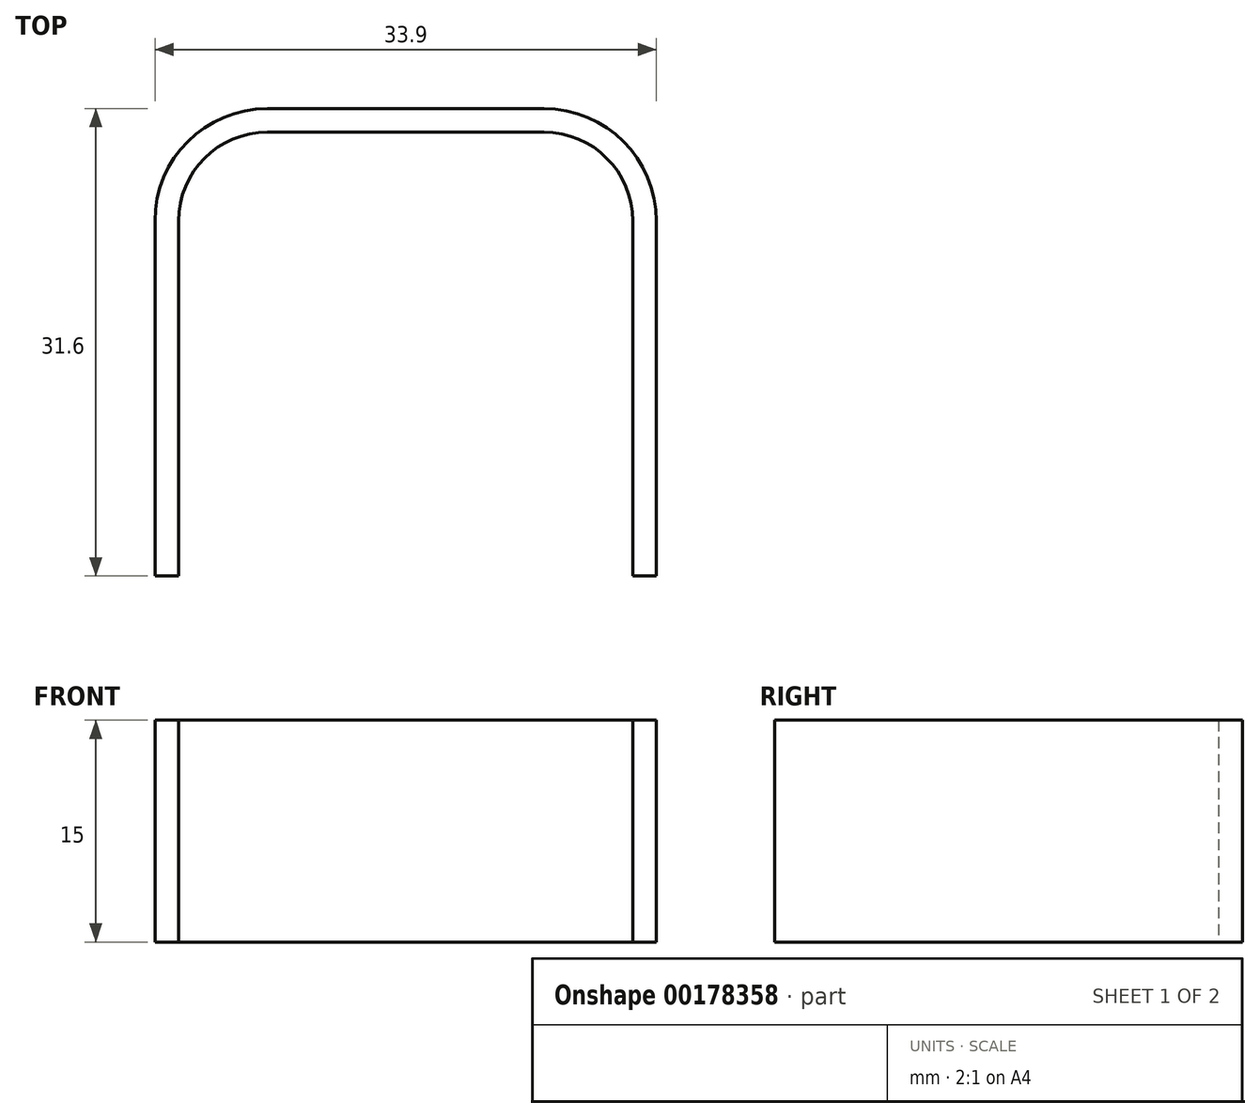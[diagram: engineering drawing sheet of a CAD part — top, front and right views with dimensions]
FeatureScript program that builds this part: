
annotation { "Feature Type Name" : "Feature", "Feature Type Description" : "" }
export const myFeature = defineFeature(function(context is Context, id is Id, definition is map)
    precondition{}
    {
        {
            var Q0;
            Q0=qCreatedBy(makeId("Top.planeOp"),FACE);
            var sketch = newSketch(context, id + "F0", { "sketchPlane" : qUnion([Q0])});
            skLineSegment(sketch, "E0", {"start": v(-15.35, -15.8) * mm, "end": v(-15.35, 14.2) * mm});
            skLineSegment(sketch, "E1", {"start": v(-15.35, 14.2) * mm, "end": v(15.35, 14.2) * mm});
            skLineSegment(sketch, "E2", {"start": v(15.35, 14.2) * mm, "end": v(15.35, -15.8) * mm});
            skLineSegment(sketch, "E3.0", {"start": v(16.95, 15.8) * mm, "end": v(16.95, -15.8) * mm});
            skLineSegment(sketch, "E3.1", {"start": v(-16.95, 15.8) * mm, "end": v(16.95, 15.8) * mm});
            skLineSegment(sketch, "E3.2", {"start": v(-16.95, -15.8) * mm, "end": v(-16.95, 15.8) * mm});
            skPoint(sketch, "E4", {"position": v(0, 15.8) * mm});
            skPoint(sketch, "E5", {"position": v(16.95, 0) * mm});
            skLineSegment(sketch, "E6", {"start": v(-16.95, -15.8) * mm, "end": v(-15.35, -15.8) * mm});
            skLineSegment(sketch, "E7", {"start": v(15.35, -15.8) * mm, "end": v(16.95, -15.8) * mm});
            skSolve(sketch);
        }
        {
            var Q0;
            Q0 = qSketchRegion(id + "F0", true);
            extrude(context, id + "F1", {"entities" : qUnion([Q0]), "depth" : 15 * mm, "offsetDistance" : 25 * mm});
        }
        {
            var Q0;
            Q0=makeQuery(id+"F1.opExtrude","SWEPT_EDGE",EDGE,{"disambiguationData":[OSD([sQuery(id+"F0.wireOp",EDGE,"E0"),sQuery(id+"F0.wireOp",EDGE,"E1")])]});
            var Q1;
            Q1=makeQuery(id+"F1.opExtrude","SWEPT_EDGE",EDGE,{"disambiguationData":[OSD([sQuery(id+"F0.wireOp",EDGE,"E1"),sQuery(id+"F0.wireOp",EDGE,"E2")])]});
            fillet(context, id + "F2", {"entities" : qUnion([Q0, Q1]), "radius" : 6 * mm, "tangentPropagation" : true, "allowEdgeOverflow" : false});
        }
        {
            var Q0;
            Q0=makeQuery(id+"F1.opExtrude","SWEPT_EDGE",EDGE,{"disambiguationData":[OSD([sQuery(id+"F0.wireOp",EDGE,"E3.1"),sQuery(id+"F0.wireOp",EDGE,"E3.2")])]});
            var Q1;
            Q1=makeQuery(id+"F1.opExtrude","SWEPT_EDGE",EDGE,{"disambiguationData":[OSD([sQuery(id+"F0.wireOp",EDGE,"E3.0"),sQuery(id+"F0.wireOp",EDGE,"E3.1")])]});
            fillet(context, id + "F3", {"entities" : qUnion([Q0, Q1]), "radius" : 7.6 * mm, "tangentPropagation" : true, "allowEdgeOverflow" : false});
        }
    });
